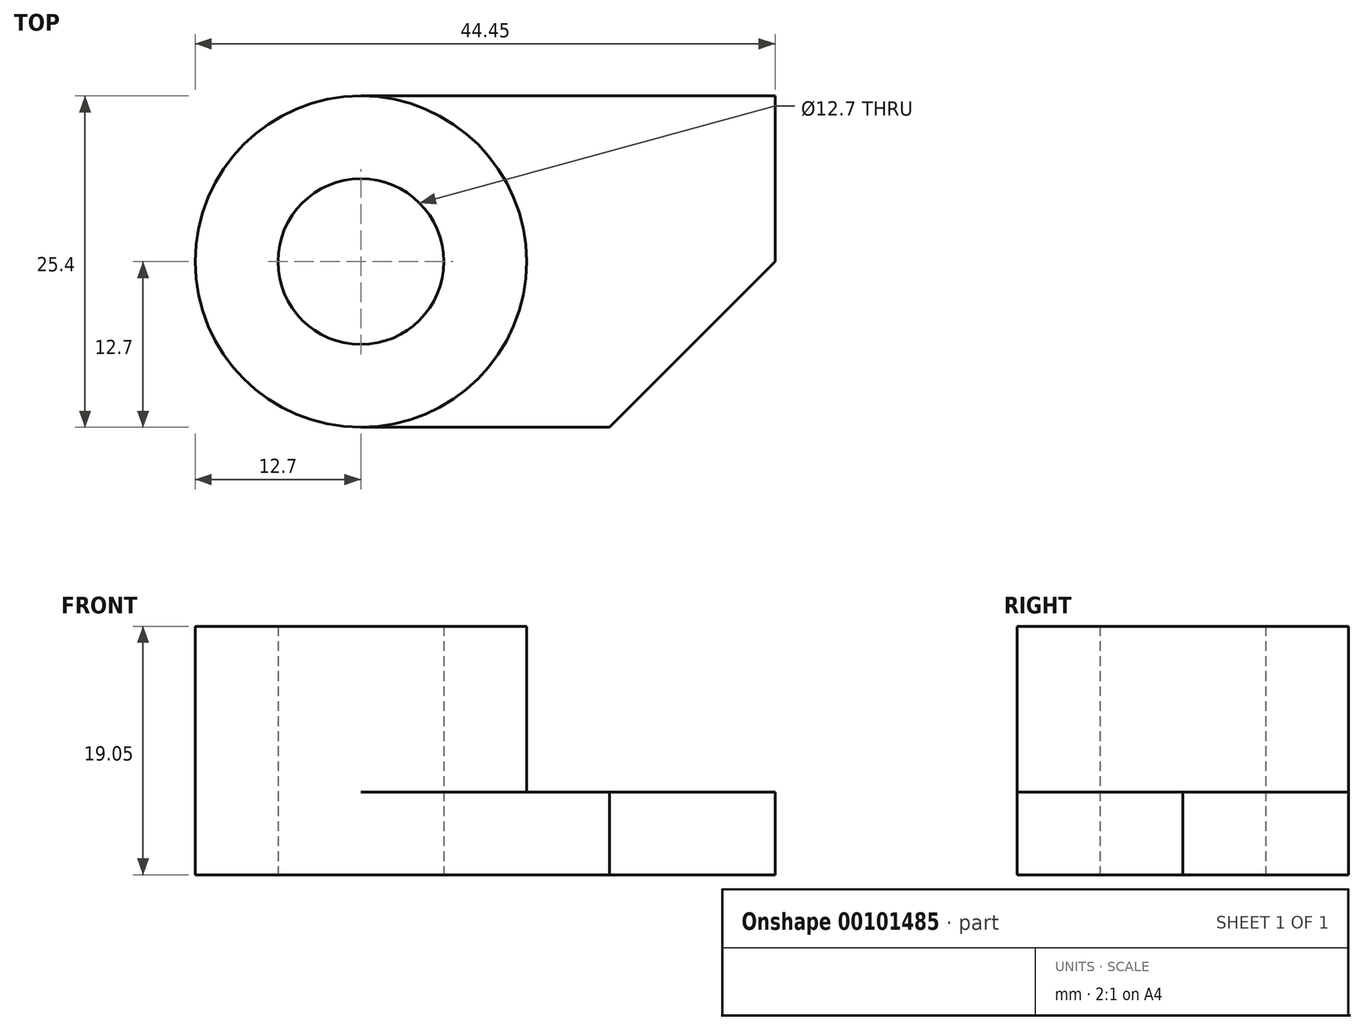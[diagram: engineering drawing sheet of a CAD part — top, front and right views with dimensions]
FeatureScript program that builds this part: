
annotation { "Feature Type Name" : "Feature", "Feature Type Description" : "" }
export const myFeature = defineFeature(function(context is Context, id is Id, definition is map)
    precondition{}
    {
        {
            var Q0;
            Q0=qCreatedBy(makeId("Top.planeOp"),FACE);
            var sketch = newSketch(context, id + "F0", { "sketchPlane" : qUnion([Q0])});
            skCircle(sketch, "E0", {"center": v(0, 0) * mm, "radius": 6.35 * mm});
            skCircle(sketch, "E1", {"center": v(0, 0) * mm, "radius": 12.7 * mm});
            skSolve(sketch);
        }
        {
            var Q0;
            Q0=makeQuery(id+"F0.imprint","IMPRINT",FACE,{"disambiguationData":[TD([[makeQuery(id+"F0.imprint","IMPRINT",EDGE,{"derivedFrom":sQuery(id+"F0.wireOp",EDGE,"E0")}),-1.0]])]});
            extrude(context, id + "F1", {"entities" : qUnion([Q0]), "depth" : 19.05 * mm});
        }
        {
            var Q0;
            Q0=qCreatedBy(makeId("Top.planeOp"),FACE);
            var sketch = newSketch(context, id + "F2", { "sketchPlane" : qUnion([Q0])});
            skLineSegment(sketch, "E2", {"start": v(0, -12.7) * mm, "end": v(19.05, -12.7) * mm});
            skLineSegment(sketch, "E3", {"start": v(19.05, -12.7) * mm, "end": v(31.75, 0) * mm});
            skLineSegment(sketch, "E4", {"start": v(31.75, 0) * mm, "end": v(31.75, 12.7) * mm});
            skLineSegment(sketch, "E5", {"start": v(31.75, 12.7) * mm, "end": v(0, 12.7) * mm});
            skArc(sketch, "E6", {"start": v(0, -12.7) * mm, "mid": v(12.7, 0) * mm, "end": v(0, 12.7) * mm});
            skSolve(sketch);
        }
        {
            var Q0;
            Q0=makeQuery(id+"F2.imprint","IMPRINT",FACE,{"disambiguationData":[TD([[makeQuery(id+"F2.imprint","IMPRINT",EDGE,{"derivedFrom":sQuery(id+"F2.wireOp",EDGE,"E2")}),1.0]])]});
            extrude(context, id + "F3", {"entities" : qUnion([Q0]), "operationType" : NewBodyOperationType.ADD, "depth" : 6.35 * mm});
        }
    });
